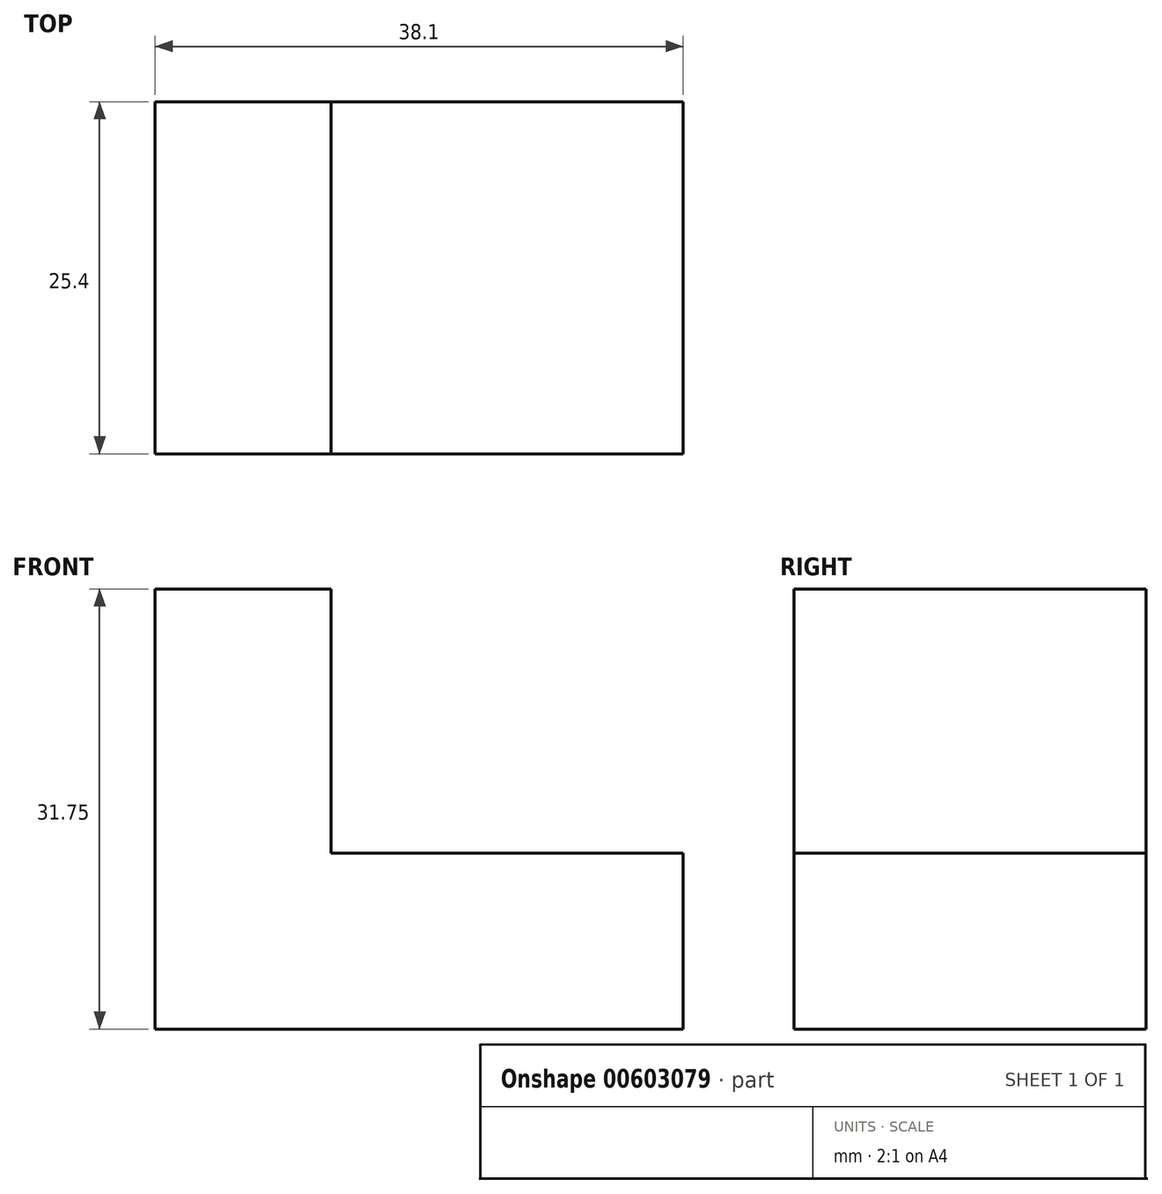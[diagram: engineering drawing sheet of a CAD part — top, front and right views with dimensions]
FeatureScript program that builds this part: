
annotation { "Feature Type Name" : "Feature", "Feature Type Description" : "" }
export const myFeature = defineFeature(function(context is Context, id is Id, definition is map)
    precondition{}
    {
        {
            var Q0;
            Q0=qCreatedBy(makeId("Front.planeOp"),FACE);
            var sketch = newSketch(context, id + "F0", { "sketchPlane" : qUnion([Q0])});
            skLineSegment(sketch, "E0", {"start": v(0, 0) * mm, "end": v(0, 31.75) * mm});
            skLineSegment(sketch, "E1", {"start": v(0, 31.75) * mm, "end": v(12.7, 31.75) * mm});
            skLineSegment(sketch, "E2", {"start": v(12.7, 31.75) * mm, "end": v(12.7, 12.7) * mm});
            skLineSegment(sketch, "E3", {"start": v(12.7, 12.7) * mm, "end": v(38.1, 12.7) * mm});
            skLineSegment(sketch, "E4", {"start": v(38.1, 12.7) * mm, "end": v(38.1, 0) * mm});
            skLineSegment(sketch, "E5", {"start": v(38.1, 0) * mm, "end": v(0, 0) * mm});
            skSolve(sketch);
        }
        {
            var Q0;
            Q0=makeQuery(id+"F0.imprint","IMPRINT",FACE,{"disambiguationData":[TD([[makeQuery(id+"F0.imprint","IMPRINT",EDGE,{"derivedFrom":sQuery(id+"F0.wireOp",EDGE,"E0")}),-1.0]])]});
            extrude(context, id + "F1", {"entities" : qUnion([Q0]), "depth" : 25.4 * mm, "offsetDistance" : 25.4 * mm});
        }
    });
